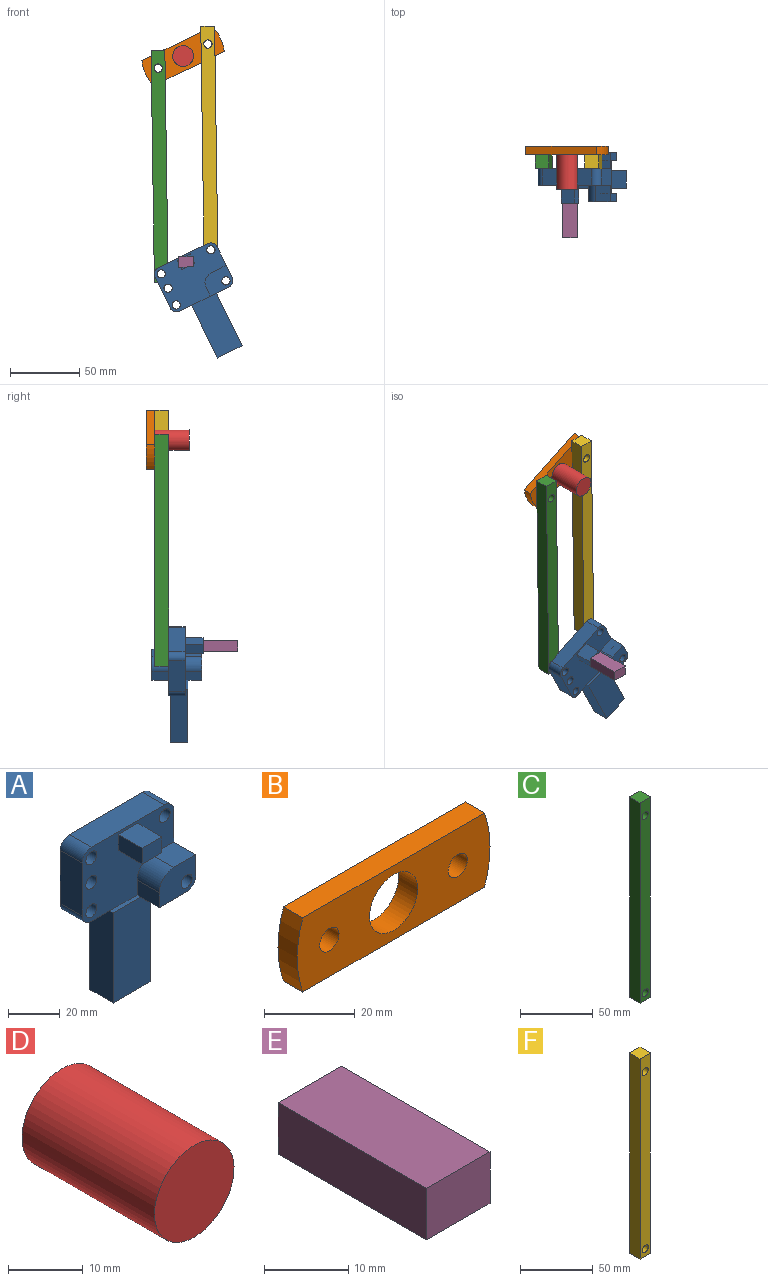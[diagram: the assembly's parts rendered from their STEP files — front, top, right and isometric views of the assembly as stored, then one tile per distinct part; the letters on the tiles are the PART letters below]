
ASSEMBLY  parts=6 mates=6
PART A: 39 faces, bbox 50x37x77.5 mm
  f0: plane 40x36mm, normal (0,0,-1), area 415.1mm2, adj f2,f3,f4,f9,f14,f17,f19,f22
  f1: plane 36x25mm, normal (1,0,0), area 340.7mm2, adj f2,f3,f4,f5,f14,f15,f19,f20
  f2: cylinder r=5mm len=6mm, axis (0,-1,0), area 47.1mm2, adj f0,f1,f19,f27
  f3: plane 50x35mm, normal (0,-1,0), area 1254.4mm2, adj f0,f1,f5,f6,f7,f8,f9,f10
  f4: cylinder r=9.69mm len=24mm, axis (0,1,0), area 617.6mm2, adj f0,f1,f26,f27
  f5: cylinder r=5mm len=12mm, axis (0,1,0), area 94.2mm2, adj f1,f3,f6,f14
  f6: plane 40x12mm, normal (0,0,1), area 480mm2, adj f3,f5,f7,f14
  f7: cylinder r=5mm len=12mm, axis (0,1,0), area 94.2mm2, adj f3,f6,f8,f14
  f8: plane 25x12mm, normal (-1,0,0), area 300mm2, adj f3,f7,f9,f14
  f9: cylinder r=5mm len=12mm, axis (0,1,0), area 94.2mm2, adj f0,f3,f8,f14
  f10: cylinder r=3mm len=12mm, axis (0,1,0), area 226.2mm2, adj f3,f14
  f11: cylinder r=3mm len=12mm, axis (0,1,0), area 226.2mm2, adj f3,f14
  f12: cylinder r=3mm len=12mm, axis (0,1,0), area 226.2mm2, adj f3,f14
  f13: cylinder r=3mm len=12mm, axis (0,1,0), area 226.2mm2, adj f3,f14
  f14: plane 50x35mm, normal (0,1,0), area 1334.5mm2, adj f0,f1,f5,f6,f7,f8,f9,f10
  f15: plane 12x12mm, normal (0,0,1), area 144mm2, adj f1,f14,f16,f19
  f16: cylinder r=8mm len=12mm, axis (0,-1,0), area 150.8mm2, adj f14,f15,f17,f19
  f17: plane 12x7mm, normal (-1,0,0), area 84mm2, adj f0,f14,f16,f19
  f18: cylinder r=3mm len=6mm, axis (0,-1,0), area 113.1mm2, adj f19,f27
  f19: plane 20x15mm, normal (0,1,0), area 252.6mm2, adj f0,f1,f2,f15,f16,f17,f18
  f20: plane 12x12mm, normal (0,0,1), area 144mm2, adj f1,f3,f21,f25
  f21: cylinder r=8mm len=12mm, axis (0,1,0), area 150.8mm2, adj f3,f20,f22,f25
  f22: plane 12x7mm, normal (-1,0,0), area 84mm2, adj f0,f3,f21,f25,f33
  f23: cylinder r=5mm len=6mm, axis (0,1,0), area 47.1mm2, adj f0,f1,f25,f26
  f24: cylinder r=3mm len=6mm, axis (0,1,0), area 113.1mm2, adj f25,f26
  f25: plane 20x15mm, normal (0,-1,0), area 252.6mm2, adj f0,f1,f20,f21,f22,f23,f24
  f26: plane 14.69x14.69mm, normal (0,1,0), area 157.6mm2, adj f0,f1,f4,f23,f24
  f27: plane 14.69x14.69mm, normal (0,-1,0), area 157.6mm2, adj f0,f1,f2,f4,f18
  f28: plane 10.67x7.51mm, normal (0,-1,0), area 80.1mm2, adj f29,f30,f31,f32
  f29: plane 13x7.51mm, normal (-1,0,0), area 97.6mm2, adj f3,f28,f30,f32
  f30: plane 13x10.67mm, normal (0,0,1), area 138.8mm2, adj f3,f28,f29,f31
  f31: plane 13x7.51mm, normal (1,0,0), area 97.6mm2, adj f3,f28,f30,f32
  f32: plane 13x10.67mm, normal (0,0,-1), area 138.8mm2, adj f3,f28,f29,f31
  f33: plane 15x2mm, normal (0,0,1), area 30mm2, adj f3,f22,f35,f36
  f34: plane 20x12.78mm, normal (0,0,-1), area 255.6mm2, adj f35,f36,f37,f38
  f35: plane 42.53x20mm, normal (0,-1,0), area 850.6mm2, adj f0,f33,f34,f36,f38
  f36: plane 42.53x12.78mm, normal (-1,0,0), area 543.5mm2, adj f0,f33,f34,f35,f37
  f37: plane 42.53x20mm, normal (0,1,0), area 850.6mm2, adj f0,f34,f36,f38
  f38: plane 42.53x12.78mm, normal (1,0,0), area 543.5mm2, adj f0,f34,f35,f37
PART B: 9 faces, bbox 60x6x20 mm
  f0: cylinder r=30mm len=20mm, axis (0,1,0), area 122.3mm2, adj f1,f2,f7,f8
  f1: plane 60x20mm, normal (0,-1,0), area 944.1mm2, adj f0,f3,f4,f5,f6,f7,f8
  f2: plane 60x20mm, normal (0,1,0), area 944.1mm2, adj f0,f3,f4,f5,f6,f7,f8
  f3: cylinder r=3mm len=6mm, axis (0,1,0), area 113.1mm2, adj f1,f2
  f4: cylinder r=7.5mm len=15mm, axis (0,1,0), area 282.7mm2, adj f1,f2
  f5: cylinder r=3mm len=6mm, axis (0,1,0), area 113.1mm2, adj f1,f2
  f6: cylinder r=30mm len=20mm, axis (0,1,0), area 122.3mm2, adj f1,f2,f7,f8
  f7: plane 56.57x6mm, normal (0,0,-1), area 339.4mm2, adj f0,f1,f2,f6
  f8: plane 56.57x6mm, normal (0,0,1), area 339.4mm2, adj f0,f1,f2,f6
PART C: 8 faces, bbox 10x10x168 mm
  f0: plane 10x10mm, normal (0,0,1), area 100mm2, adj f1,f3,f6,f7
  f1: plane 168x10mm, normal (-1,0,0), area 1680mm2, adj f0,f2,f6,f7
  f2: plane 10x10mm, normal (0,0,-1), area 100mm2, adj f1,f3,f6,f7
  f3: plane 168x10mm, normal (1,0,0), area 1680mm2, adj f0,f2,f6,f7
  f4: cylinder r=3mm len=10mm, axis (0,1,0), area 188.5mm2, adj f6,f7
  f5: cylinder r=3mm len=10mm, axis (0,1,0), area 188.5mm2, adj f6,f7
  f6: plane 168x10mm, normal (0,-1,0), area 1623.5mm2, adj f0,f1,f2,f3,f4,f5
  f7: plane 168x10mm, normal (0,1,0), area 1623.5mm2, adj f0,f1,f2,f3,f4,f5
PART D: 3 faces, bbox 15x25x15 mm
  f0: cylinder r=7.5mm len=25mm, axis (0,1,0), area 1178.1mm2, adj f1,f2
  f1: plane 15x15mm, normal (0,-1,0), area 176.7mm2, adj f0
  f2: plane 15x15mm, normal (0,1,0), area 176.7mm2, adj f0
PART E: 6 faces, bbox 10.7x25x7.5 mm
  f0: plane 25x10.67mm, normal (0,0,-1), area 266.9mm2, adj f1,f3,f4,f5
  f1: plane 25x7.51mm, normal (1,0,0), area 187.6mm2, adj f0,f2,f4,f5
  f2: plane 25x10.67mm, normal (0,0,1), area 266.9mm2, adj f1,f3,f4,f5
  f3: plane 25x7.51mm, normal (-1,0,0), area 187.6mm2, adj f0,f2,f4,f5
  f4: plane 10.67x7.51mm, normal (0,-1,0), area 80.1mm2, adj f0,f1,f2,f3
  f5: plane 10.67x7.51mm, normal (0,1,0), area 80.1mm2, adj f0,f1,f2,f3
PART F: 8 faces, bbox 10x10x168 mm
  f0: plane 168x10mm, normal (1,0,0), area 1680mm2, adj f1,f4,f6,f7
  f1: plane 10x10mm, normal (0,0,1), area 100mm2, adj f0,f2,f6,f7
  f2: plane 168x10mm, normal (-1,0,0), area 1680mm2, adj f1,f4,f6,f7
  f3: cylinder r=3mm len=10mm, axis (0,1,0), area 188.5mm2, adj f6,f7
  f4: plane 10x10mm, normal (0,0,-1), area 100mm2, adj f0,f2,f6,f7
  f5: cylinder r=3mm len=10mm, axis (0,1,0), area 188.5mm2, adj f6,f7
  f6: plane 168x10mm, normal (0,-1,0), area 1623.5mm2, adj f0,f1,f2,f3,f4,f5
  f7: plane 168x10mm, normal (0,1,0), area 1623.5mm2, adj f0,f1,f2,f3,f4,f5
PLACE A rot(axis=(0,-1,0),25.8deg) t=(16.77,6,-8.13)mm
PLACE B rot(axis=(0,-1,0),25.8deg) t=(74.52,6,17.09)mm
PLACE C rot(axis=(0,-1,0),0.8deg) t=(4.47,6,-8.41)mm
PLACE D at identity fixed
PLACE E rot(axis=(1,0,0.01),180deg) t=(1.67,-101,55.58)mm fixed
PLACE F rot(axis=(0,-1,0),0.8deg) t=(0.48,6,8.44)mm
MATE revolute B.f3 <-> C.f4  axis (0,1,0) through (-18,0,162.32)mm
MATE revolute A.f7 <-> C.f5  axis (0,1,0) through (-15.84,-10,13.33)mm
MATE revolute D.f0 <-> B.f0  axis (0,1,0) through (0,0,171.03)mm
MATE revolute A.f5 <-> F.f3  axis (0,1,0) through (20.16,-10,30.76)mm
MATE revolute A.f28 <-> E.f4  axis (0,-1,0) through (2.16,-35,22.05)mm
MATE revolute B.f5 <-> F.f5  axis (0,-1,0) through (18,0,179.75)mm
